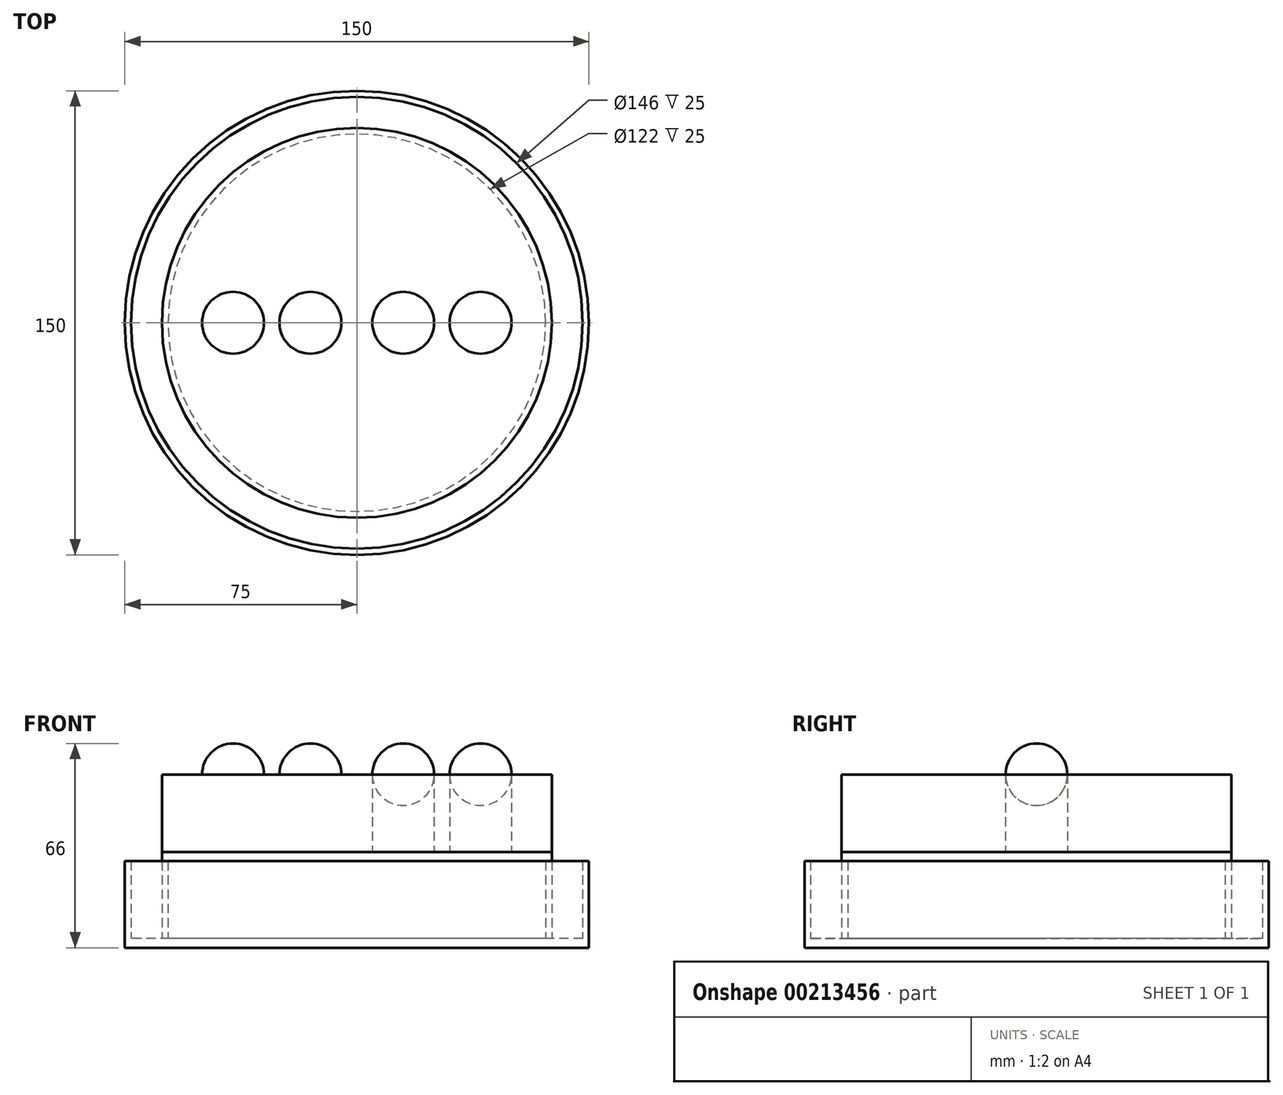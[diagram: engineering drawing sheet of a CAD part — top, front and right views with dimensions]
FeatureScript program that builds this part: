
annotation { "Feature Type Name" : "Feature", "Feature Type Description" : "" }
export const myFeature = defineFeature(function(context is Context, id is Id, definition is map)
    precondition{}
    {
        {
            var Q0;
            Q0=qCreatedBy(makeId("Top.planeOp"),FACE);
            var sketch = newSketch(context, id + "F0", { "sketchPlane" : qUnion([Q0])});
            skCircle(sketch, "E0", {"center": v(0, 0) * mm, "radius": 75 * mm});
            skCircle(sketch, "E1.0", {"center": v(0, 0) * mm, "radius": 73 * mm});
            skCircle(sketch, "E2.0", {"center": v(0, 0) * mm, "radius": 63 * mm});
            skCircle(sketch, "E3.0", {"center": v(0, 0) * mm, "radius": 61 * mm});
            skSolve(sketch);
        }
        {
            var Q0;
            Q0=makeQuery(id+"F0.imprint","IMPRINT",FACE,{"disambiguationData":[TD([[makeQuery(id+"F0.imprint","IMPRINT",EDGE,{"derivedFrom":sQuery(id+"F0.wireOp",EDGE,"E0")}),1.0]])]});
            var Q1;
            Q1=makeQuery(id+"F0.imprint","IMPRINT",FACE,{"disambiguationData":[TD([[makeQuery(id+"F0.imprint","IMPRINT",EDGE,{"derivedFrom":sQuery(id+"F0.wireOp",EDGE,"E1.0")}),1.0]])]});
            var Q2;
            Q2=makeQuery(id+"F0.imprint","IMPRINT",FACE,{"disambiguationData":[TD([[makeQuery(id+"F0.imprint","IMPRINT",EDGE,{"derivedFrom":sQuery(id+"F0.wireOp",EDGE,"E2.0")}),1.0]])]});
            extrude(context, id + "F1", {"entities" : qUnion([Q0, Q1, Q2]), "depth" : 3 * mm});
        }
        {
            var Q0;
            Q0=makeQuery(id+"F1.opExtrude","CAP_FACE",FACE,{"disambiguationData":[OSD([sQuery(id+"F0.wireOp",EDGE,"E0"),sQuery(id+"F0.wireOp",EDGE,"E3.0")])],"isStart":false});
            var sketch = newSketch(context, id + "F2", { "sketchPlane" : qUnion([Q0])});
            skCircle(sketch, "E4.0", {"center": v(0, 0) * mm, "radius": 75 * mm});
            skCircle(sketch, "E5.0", {"center": v(0, 0) * mm, "radius": 73 * mm});
            skCircle(sketch, "E6.0", {"center": v(0, 0) * mm, "radius": 63 * mm});
            skSolve(sketch);
        }
        {
            var Q0;
            Q0=makeQuery(id+"F2.imprint","IMPRINT",FACE,{"disambiguationData":[TD([[makeQuery(id+"F2.imprint","IMPRINT",EDGE,{"derivedFrom":sQuery(id+"F2.wireOp",EDGE,"E4.0")}),1.0]])]});
            var Q1;
            Q1=makeQuery(id+"F2.imprint","IMPRINT",FACE,{"disambiguationData":[TD([[makeQuery(id+"F2.imprint","IMPRINT",EDGE,{"derivedFrom":sQuery(id+"F2.wireOp",EDGE,"E6.0")}),1.0]])]});
            extrude(context, id + "F3", {"entities" : qUnion([Q0, Q1]), "operationType" : NewBodyOperationType.ADD, "depth" : 25 * mm});
        }
        {
            var Q0;
            Q0=makeQuery(id+"F0.imprint","IMPRINT",FACE,{"disambiguationData":[TD([[makeQuery(id+"F0.imprint","IMPRINT",EDGE,{"derivedFrom":sQuery(id+"F0.wireOp",EDGE,"E3.0")}),1.0]])]});
            extrude(context, id + "F4", {"entities" : qUnion([Q0]), "operationType" : NewBodyOperationType.ADD, "depth" : 3 * mm});
        }
        {
            var Q0;
            Q0=makeQuery(id+"F3.opExtrude","CAP_FACE",FACE,{"disambiguationData":[OSD([sQuery(id+"F0.wireOp",EDGE,"E3.0"),sQuery(id+"F2.wireOp",EDGE,"E6.0")])],"isStart":false});
            var sketch = newSketch(context, id + "F5", { "sketchPlane" : qUnion([Q0])});
            skCircle(sketch, "E7.0.0", {"center": v(0, 0) * mm, "radius": 61 * mm});
            skCircle(sketch, "E8.0", {"center": v(0, 0) * mm, "radius": 63 * mm});
            skSolve(sketch);
        }
        {
            var Q0;
            Q0=makeQuery(id+"F5.imprint","IMPRINT",FACE,{"disambiguationData":[TD([[makeQuery(id+"F5.imprint","IMPRINT",EDGE,{"derivedFrom":sQuery(id+"F5.wireOp",EDGE,"E7.0.0")}),-1.0]])]});
            var Q1;
            Q1=makeQuery(id+"F5.imprint","IMPRINT",FACE,{"disambiguationData":[TD([[makeQuery(id+"F5.imprint","IMPRINT",EDGE,{"derivedFrom":sQuery(id+"F5.wireOp",EDGE,"E7.0.0")}),1.0]])]});
            extrude(context, id + "F6", {"entities" : qUnion([Q0, Q1]), "operationType" : NewBodyOperationType.ADD, "depth" : 3 * mm});
        }
        {
            var Q0;
            Q0=makeQuery(id+"F6.opExtrude","CAP_FACE",FACE,{"disambiguationData":[OSD([sQuery(id+"F5.wireOp",EDGE,"E8.0")])],"isStart":false});
            var sketch = newSketch(context, id + "F7", { "sketchPlane" : qUnion([Q0])});
            skCircle(sketch, "E9", {"center": v(-40, 0) * mm, "radius": 10 * mm});
            skCircle(sketch, "E10", {"center": v(-15, 0) * mm, "radius": 10 * mm});
            skCircle(sketch, "E11.MirrorC", {"center": v(15, 0) * mm, "radius": 10 * mm});
            skCircle(sketch, "E12.MirrorC", {"center": v(40, 0) * mm, "radius": 10 * mm});
            skSolve(sketch);
        }
        {
            var Q0;
            Q0=makeQuery(id+"F7.imprint","IMPRINT",FACE,{"disambiguationData":[TD([[makeQuery(id+"F7.imprint","IMPRINT",EDGE,{"derivedFrom":sQuery(id+"F7.wireOp",EDGE,"E9")}),1.0]])]});
            var Q1;
            Q1=makeQuery(id+"F7.imprint","IMPRINT",FACE,{"disambiguationData":[TD([[makeQuery(id+"F7.imprint","IMPRINT",EDGE,{"derivedFrom":sQuery(id+"F7.wireOp",EDGE,"E10")}),1.0]])]});
            var Q2;
            Q2=makeQuery(id+"F7.imprint","IMPRINT",FACE,{"disambiguationData":[TD([[makeQuery(id+"F7.imprint","IMPRINT",EDGE,{"derivedFrom":sQuery(id+"F7.wireOp",EDGE,"E11.MirrorC")}),-1.0]])]});
            var Q3;
            Q3=makeQuery(id+"F7.imprint","IMPRINT",FACE,{"disambiguationData":[TD([[makeQuery(id+"F7.imprint","IMPRINT",EDGE,{"derivedFrom":sQuery(id+"F7.wireOp",EDGE,"E12.MirrorC")}),-1.0]])]});
            extrude(context, id + "F8", {"entities" : qUnion([Q0, Q1, Q2, Q3]), "depth" : 25 * mm});
        }
        {
            var Q0;
            Q0=qCreatedBy(makeId("Front.planeOp"),FACE);
            var sketch = newSketch(context, id + "F9", { "sketchPlane" : qUnion([Q0])});
            skLineSegment(sketch, "E13.0", {"start": v(-50, 56) * mm, "end": v(-30, 56) * mm});
            skLineSegment(sketch, "E14.0", {"start": v(-25, 56) * mm, "end": v(-5, 56) * mm});
            skLineSegment(sketch, "E15.0", {"start": v(25, 56) * mm, "end": v(5, 56) * mm});
            skLineSegment(sketch, "E16.0", {"start": v(50, 56) * mm, "end": v(30, 56) * mm});
            skArc(sketch, "E17", {"start": v(-30, 56) * mm, "mid": v(-40, 66) * mm, "end": v(-50, 56) * mm});
            skArc(sketch, "E18", {"start": v(-5, 56) * mm, "mid": v(-15, 66) * mm, "end": v(-25, 56) * mm});
            skArc(sketch, "E19.MirrorCS", {"start": v(5, 56) * mm, "mid": v(15, 66) * mm, "end": v(25, 56) * mm});
            skArc(sketch, "E20.MirrorCS", {"start": v(30, 56) * mm, "mid": v(40, 66) * mm, "end": v(50, 56) * mm});
            skSolve(sketch);
        }
        {
            var Q0;
            Q0=makeQuery(id+"F9.imprint","IMPRINT",FACE,{"disambiguationData":[TD([[makeQuery(id+"F9.imprint","IMPRINT",EDGE,{"derivedFrom":sQuery(id+"F9.wireOp",EDGE,"E13.0")}),1.0]])]});
            var Q1;
            Q1=sQuery(id+"F9.wireOp",EDGE,"E13.0");
            revolve(context, id + "F10", {"operationType" : NewBodyOperationType.ADD, "entities" : qUnion([Q0]), "axis" : qUnion([Q1]), "revolveType" : RevolveType.FULL});
        }
        {
            var Q0;
            Q0=makeQuery(id+"F9.imprint","IMPRINT",FACE,{"disambiguationData":[TD([[makeQuery(id+"F9.imprint","IMPRINT",EDGE,{"derivedFrom":sQuery(id+"F9.wireOp",EDGE,"E14.0")}),1.0]])]});
            var Q1;
            Q1=sQuery(id+"F9.wireOp",EDGE,"E14.0");
            revolve(context, id + "F11", {"operationType" : NewBodyOperationType.ADD, "entities" : qUnion([Q0]), "axis" : qUnion([Q1]), "revolveType" : RevolveType.FULL});
        }
        {
            var Q0;
            Q0=makeQuery(id+"F9.imprint","IMPRINT",FACE,{"disambiguationData":[TD([[makeQuery(id+"F9.imprint","IMPRINT",EDGE,{"derivedFrom":sQuery(id+"F9.wireOp",EDGE,"E15.0")}),-1.0]])]});
            var Q1;
            Q1=sQuery(id+"F9.wireOp",EDGE,"E15.0");
            revolve(context, id + "F12", {"operationType" : NewBodyOperationType.ADD, "entities" : qUnion([Q0]), "axis" : qUnion([Q1]), "revolveType" : RevolveType.FULL});
        }
        {
            var Q0;
            Q0=makeQuery(id+"F9.imprint","IMPRINT",FACE,{"disambiguationData":[TD([[makeQuery(id+"F9.imprint","IMPRINT",EDGE,{"derivedFrom":sQuery(id+"F9.wireOp",EDGE,"E16.0")}),-1.0]])]});
            var Q1;
            Q1=sQuery(id+"F9.wireOp",EDGE,"E16.0");
            revolve(context, id + "F13", {"operationType" : NewBodyOperationType.ADD, "entities" : qUnion([Q0]), "axis" : qUnion([Q1]), "revolveType" : RevolveType.FULL});
        }
    });
